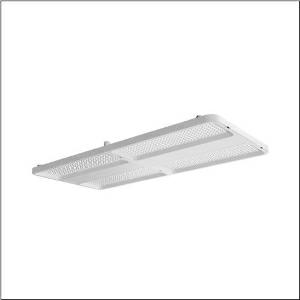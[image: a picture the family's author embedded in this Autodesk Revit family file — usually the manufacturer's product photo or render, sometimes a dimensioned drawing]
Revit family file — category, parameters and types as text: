
# Revit family: highbay_11_maxi_51hn12db4qda
name_source: partatom
category: Lighting Fixtures
units: mm (PartAtom-declared; Revit-internal decimal feet)

## family parameters
Cut with Voids When Loaded = No
Host = Face
Light Source = No
Part Type = Normal
Room Calculation Point = No
Round Connector Dimension = Use Diameter
Shared = No

## types (1)
- --- (1 x LED, 5620 lm, 27.8 W, 4000K)
    Apparent Load = 28 VA
    CIE Flux Codes = 87 98 100 100 100
    Color Rendering = 80
    Color Temperature = 4000K
    Default Elevation = 1800 mm
    Description = high bay luminaire Highbay 11 maxi; direct symmetric wide distribution, light control with lens of PMMA; UGR ≤ 22 (X = 4H | Y = 8H | S = 0.25H | reflection values 70/50/20); luminous flux: 36.000lm; light colour: 840, colour temperature: 4000K, MacAdam ≤ 2 SDCM (initial), colour rendering: CRI > 80; luminous efficacy: 202,6lm/W; rated service life: 100.000h (L95) at AT= 25°C; control: DALI 2; luminaire connection: terminal, 5-pole, max. 2.5mm² (cable entry for one cable, Ø 8.5..16mm); mains connection: 230..240V, AC/DC 0/50..60Hz; connected load: 177,7W; protection rating (complete): IP66; insulation class (complete): insulation class I (protective earthing); protection symbol: D; impact resistance: IK08; certification: CE, ENEC, VDE, UKCA; luminaire for central battery installations according to EN 60598-2-22, internal wiring halogen-free; luminaire Suitable for use in the food industry according to the specifications of IFS-Food, HACCP and/or BRC; LABS conformity tested according to VDMA 24364:2018-05; housing frame of high-performance plastic PA6, matt traffic white (RAL 9016); cover of PMMA; dimension (LxWxH): 946 x 442 x 72mm; permissible operating ambient temperature: -40..+55°C (reducing of maximum allowable ambient temperature of 5°C with ceiling mounting); packaging unit: 1 piece; (delivery without accessories; please order mounting accessories separately)
    Height = 72 mm  [stored 0.23622 ft]
    Lamp = 1 x LED
    Lamp Light Flux = 5620 lm
    Lamp Power = 27.8 W
    Lamp count = 1
    Length = 946 mm
    Luminous efficacy = 202 lm/W
    Manufacturer = Siteco
    ModVariant = No
    Model = 51HN12DB4QDA
    Mounting Place = Ceiling
    Mounting Type = Pendant
    Number of Poles = 1
    OnlyDefault = Yes
    Power Factor = 1
    Product Name = Highbay 11 maxi
    Product group = high bay luminaire
    ProductGroupID = 902
    Protection Class = Protection class I
    Protection Degree = IP 66
    RLX_Detail_Level = 1
    RLX_Emergency_Light_Flux = 0 lm
    RLX_Emergency_Type = 0
    RLX_Emergency_Type_DB = No
    RlxData = <blob elided: 126977 chars, md5=1d46e99c>
    Socket = socket
    Standby Power = 0 W
    System Light Flux = 5620 lm
    System Power = 28 W
    Type Comments = : DC mode (central or group accumulator) initial emergency light level
    Type Image = l_1363244.jpg
    URL = http://relux.com
    VarID = @adj_024889
    Voltage = 0 V
    Weight = 0.00 kg
    Width = 442 mm

note: [stored X ft] marks values corroborated as IEEE doubles in the binary element streams (Revit-internal decimal feet)

## geometry (parser evidence)
native form markers: Blend x4, Sweep x10
no freeform markers — native parametric forms only
